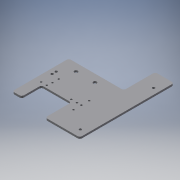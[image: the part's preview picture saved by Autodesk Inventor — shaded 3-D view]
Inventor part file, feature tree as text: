
AUTODESK INVENTOR PART (.ipt)
format: ipt  version: 2016 (Build 200138000, 138)  size: 164,352 bytes
history: native  units: mm
features: reference x15, sketch x5, extrude x4, plane x1, fillet x1
ambient origin geometry x8: Origin, YZ Plane, XZ Plane, XY Plane, X Axis, Y Axis, Z Axis, Center Point
bodies: Solid1 (feature_tree)
feature tree (26):
  plane  "Work Plane1"
  extrude  "Extrusion1"  Depth=6.0mm TaperAngle=0.0deg
  fillet  "Fillet1"  Radius=95.0mm
  sketch  "Sketch2"  dims[d5=63.0mm d6=30.0mm]
  extrude  "Extrusion3"  Depth=30.0mm
  extrude  "Extrusion4"  Depth=300.0mm
  extrude  "Extrusion5"  Depth=100.0mm
  sketch  "Sketch1"  dims[d0=110.0mm d2=6.0mm d3=0.0mm d4=95.0mm]
  sketch  "Sketch3"  dims[d7=180.0mm d10=300.0mm]
  reference  "Reference1"
  reference  "Reference2"
  sketch  "Sketch4"  dims[d11=7.0mm d15=100.0mm]
  reference  "Reference3"
  reference  "Reference4"
  reference  "Reference5"
  reference  "Reference6"
  sketch  "Sketch5"  dims[d17=8.0mm d18=60.0mm d19=60.0mm d27=30.0mm d30=0.0mm d31=0.0mm d32=10.0mm d33=0.0mm d34=0.0mm d35=0.0mm]
  reference  "Reference7"
  reference  "Reference8"
  reference  "Reference9"
  reference  "Reference10"
  reference  "Reference11"
  reference  "Reference12"
  reference  "Reference13"
  reference  "Reference14"
  reference  "Reference15"
